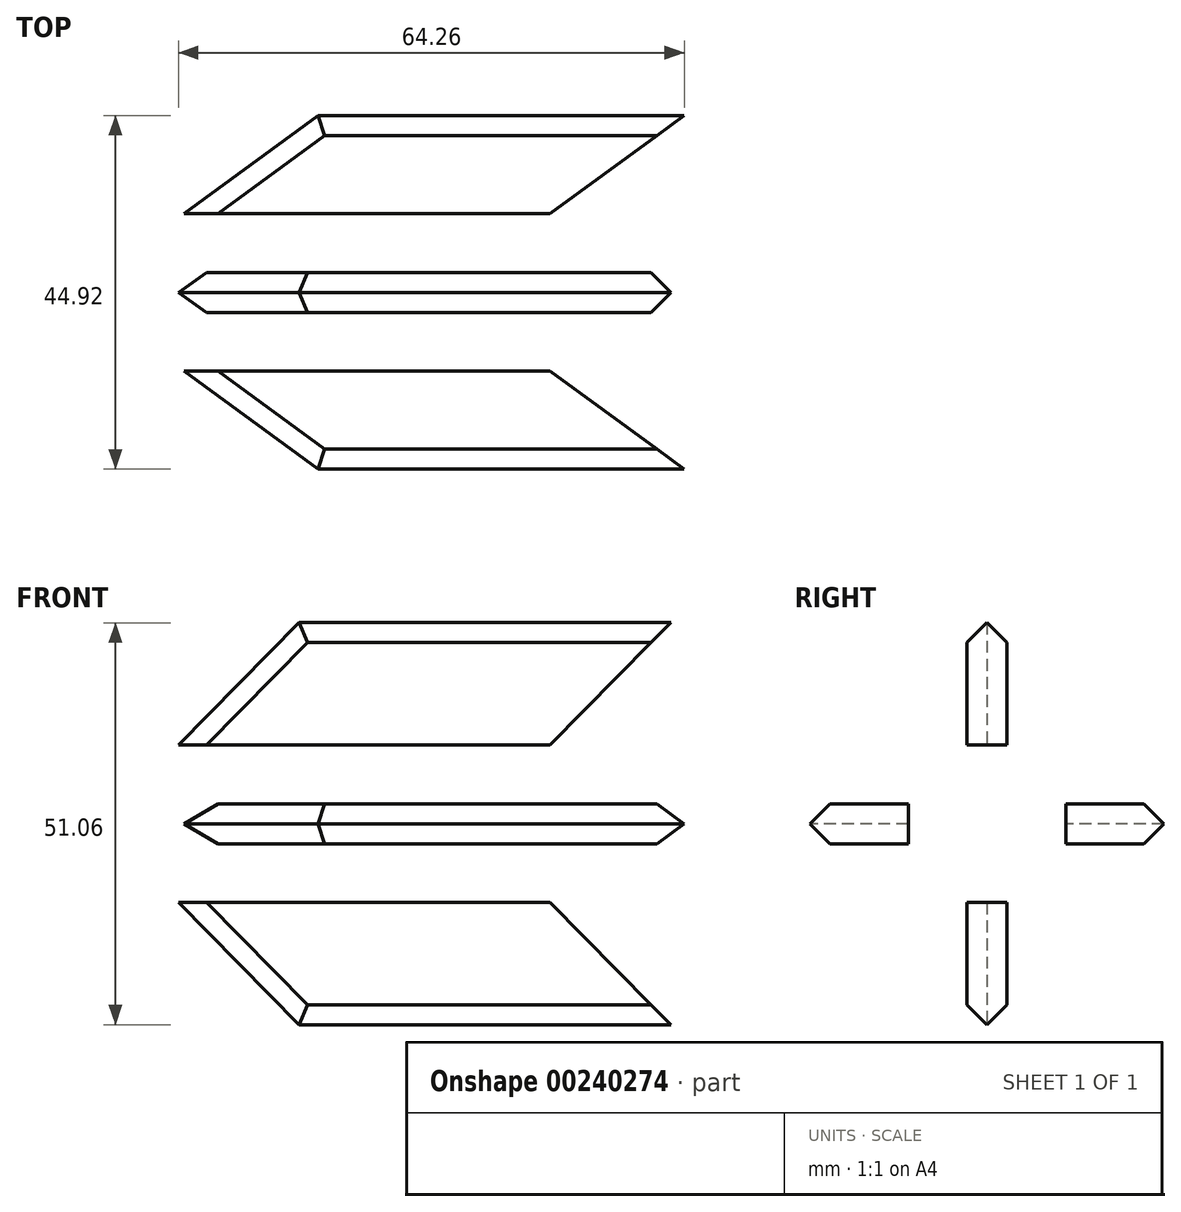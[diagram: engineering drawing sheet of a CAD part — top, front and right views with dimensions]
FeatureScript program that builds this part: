
annotation { "Feature Type Name" : "Feature", "Feature Type Description" : "" }
export const myFeature = defineFeature(function(context is Context, id is Id, definition is map)
    precondition{}
    {
        {
            var Q0;
            Q0=qCreatedBy(makeId("Top.planeOp"),FACE);
            var sketch = newSketch(context, id + "F0", { "sketchPlane" : qUnion([Q0])});
            skLineSegment(sketch, "E0.bottom", {"start": v(25.4, 10) * mm, "end": v(-25.4, 10) * mm});
            skLineSegment(sketch, "E0.top", {"start": v(25.4, -10) * mm, "end": v(-25.4, -10) * mm});
            skLineSegment(sketch, "E0.left", {"start": v(25.4, 10) * mm, "end": v(25.4, -10) * mm});
            skLineSegment(sketch, "E0.right", {"start": v(-25.4, 10) * mm, "end": v(-25.4, -10) * mm});
            skPoint(sketch, "E0.middle", {"position": v(0, 0) * mm});
            skLineSegment(sketch, "E1", {"start": v(89.65, 0) * mm, "end": v(-83.29, 0) * mm});
            skPoint(sketch, "E1.endSnap0", {"position": v(-25.4, 0) * mm});
            skLineSegment(sketch, "E2", {"start": v(-25.4, 10) * mm, "end": v(-4.9, 25) * mm});
            skLineSegment(sketch, "E3", {"start": v(-4.9, 25) * mm, "end": v(45.9, 25) * mm});
            skLineSegment(sketch, "E4", {"start": v(45.9, 25) * mm, "end": v(25.4, 10) * mm});
            skLineSegment(sketch, "E5.MirrorCS", {"start": v(-25.4, -10) * mm, "end": v(-4.9, -25) * mm});
            skLineSegment(sketch, "E6.MirrorCS", {"start": v(-4.9, -25) * mm, "end": v(45.9, -25) * mm});
            skLineSegment(sketch, "E7.MirrorCS", {"start": v(45.9, -25) * mm, "end": v(25.4, -10) * mm});
            skSolve(sketch);
        }
        {
            var Q0;
            Q0=qCreatedBy(makeId("Front.planeOp"),FACE);
            var sketch = newSketch(context, id + "F1", { "sketchPlane" : qUnion([Q0])});
            skLineSegment(sketch, "E8.bottom", {"start": v(25.4, 10) * mm, "end": v(-25.4, 10) * mm});
            skLineSegment(sketch, "E8.top", {"start": v(25.4, -10) * mm, "end": v(-25.4, -10) * mm});
            skLineSegment(sketch, "E8.left", {"start": v(25.4, 10) * mm, "end": v(25.4, -10) * mm});
            skLineSegment(sketch, "E8.right", {"start": v(-25.4, 10) * mm, "end": v(-25.4, -10) * mm});
            skPoint(sketch, "E8.middle", {"position": v(0, 0) * mm});
            skLineSegment(sketch, "E9", {"start": v(-25.4, 10) * mm, "end": v(-7.55, 28.07) * mm});
            skLineSegment(sketch, "E10", {"start": v(-7.55, 28.07) * mm, "end": v(43.25, 28.07) * mm});
            skLineSegment(sketch, "E11", {"start": v(43.25, 28.07) * mm, "end": v(25.4, 10) * mm});
            skLineSegment(sketch, "E12.MirrorCS", {"start": v(-25.4, -10) * mm, "end": v(-7.55, -28.07) * mm});
            skLineSegment(sketch, "E13.MirrorCS", {"start": v(-7.55, -28.07) * mm, "end": v(43.25, -28.07) * mm});
            skLineSegment(sketch, "E14.MirrorCS", {"start": v(43.25, -28.07) * mm, "end": v(25.4, -10) * mm});
            skSolve(sketch);
        }
        {
            var Q0;
            Q0=makeQuery(id+"F0.imprint","IMPRINT",FACE,{"disambiguationData":[TD([[makeQuery(id+"F0.imprint","IMPRINT",EDGE,{"derivedFrom":sQuery(id+"F0.wireOp",EDGE,"E0.bottom")}),-1.0]])]});
            var Q1;
            Q1=makeQuery(id+"F0.imprint","IMPRINT",FACE,{"disambiguationData":[TD([[makeQuery(id+"F0.imprint","IMPRINT",EDGE,{"derivedFrom":sQuery(id+"F0.wireOp",EDGE,"E0.top")}),1.0]])]});
            extrude(context, id + "F2", {"entities" : qUnion([Q0, Q1]), "endBound" : BoundingType.SYMMETRIC, "depth" : 5.08 * mm});
        }
        {
            var Q0;
            Q0=makeQuery(id+"F1.imprint","IMPRINT",FACE,{"disambiguationData":[TD([[makeQuery(id+"F1.imprint","IMPRINT",EDGE,{"derivedFrom":sQuery(id+"F1.wireOp",EDGE,"E8.bottom")}),-1.0]])]});
            var Q1;
            Q1=makeQuery(id+"F1.imprint","IMPRINT",FACE,{"disambiguationData":[TD([[makeQuery(id+"F1.imprint","IMPRINT",EDGE,{"derivedFrom":sQuery(id+"F1.wireOp",EDGE,"E8.top")}),1.0]])]});
            extrude(context, id + "F3", {"entities" : qUnion([Q0, Q1]), "endBound" : BoundingType.SYMMETRIC, "depth" : 5.08 * mm});
        }
        {
            var Q0;
            Q0=makeQuery(id+"F2.opExtrude","CAP_EDGE",EDGE,{"disambiguationData":[OSD([sQuery(id+"F0.wireOp",EDGE,"E6.MirrorCS")])],"isStart":true});
            var Q1;
            Q1=makeQuery(id+"F2.opExtrude","CAP_EDGE",EDGE,{"disambiguationData":[OSD([sQuery(id+"F0.wireOp",EDGE,"E6.MirrorCS")])],"isStart":false});
            var Q2;
            Q2=makeQuery(id+"F3.opExtrude","CAP_EDGE",EDGE,{"disambiguationData":[OSD([sQuery(id+"F1.wireOp",EDGE,"E10")])],"isStart":true});
            var Q3;
            Q3=makeQuery(id+"F3.opExtrude","CAP_EDGE",EDGE,{"disambiguationData":[OSD([sQuery(id+"F1.wireOp",EDGE,"E10")])],"isStart":false});
            var Q4;
            Q4=makeQuery(id+"F2.opExtrude","CAP_EDGE",EDGE,{"disambiguationData":[OSD([sQuery(id+"F0.wireOp",EDGE,"E3")])],"isStart":false});
            var Q5;
            Q5=makeQuery(id+"F2.opExtrude","CAP_EDGE",EDGE,{"disambiguationData":[OSD([sQuery(id+"F0.wireOp",EDGE,"E3")])],"isStart":true});
            var Q6;
            Q6=makeQuery(id+"F3.opExtrude","CAP_EDGE",EDGE,{"disambiguationData":[OSD([sQuery(id+"F1.wireOp",EDGE,"E13.MirrorCS")])],"isStart":true});
            var Q7;
            Q7=makeQuery(id+"F3.opExtrude","CAP_EDGE",EDGE,{"disambiguationData":[OSD([sQuery(id+"F1.wireOp",EDGE,"E13.MirrorCS")])],"isStart":false});
            chamfer(context, id + "F4", {"entities" : qUnion([Q0, Q1, Q2, Q3, Q4, Q5, Q6, Q7]), "width" : 5.08 * mm, "tangentPropagation" : true});
        }
        {
            var Q0;
            Q0=makeQuery(id+"F3.opExtrude","CAP_EDGE",EDGE,{"disambiguationData":[OSD([sQuery(id+"F1.wireOp",EDGE,"E12.MirrorCS")])],"isStart":true});
            var Q1;
            Q1=makeQuery(id+"F3.opExtrude","CAP_EDGE",EDGE,{"disambiguationData":[OSD([sQuery(id+"F1.wireOp",EDGE,"E12.MirrorCS")])],"isStart":false});
            var Q2;
            Q2=makeQuery(id+"F2.opExtrude","CAP_EDGE",EDGE,{"disambiguationData":[OSD([sQuery(id+"F0.wireOp",EDGE,"E2")])],"isStart":true});
            var Q3;
            Q3=makeQuery(id+"F2.opExtrude","CAP_EDGE",EDGE,{"disambiguationData":[OSD([sQuery(id+"F0.wireOp",EDGE,"E2")])],"isStart":false});
            var Q4;
            Q4=makeQuery(id+"F3.opExtrude","CAP_EDGE",EDGE,{"disambiguationData":[OSD([sQuery(id+"F1.wireOp",EDGE,"E9")])],"isStart":true});
            var Q5;
            Q5=makeQuery(id+"F3.opExtrude","CAP_EDGE",EDGE,{"disambiguationData":[OSD([sQuery(id+"F1.wireOp",EDGE,"E9")])],"isStart":false});
            var Q6;
            Q6=makeQuery(id+"F2.opExtrude","CAP_EDGE",EDGE,{"disambiguationData":[OSD([sQuery(id+"F0.wireOp",EDGE,"E5.MirrorCS")])],"isStart":false});
            var Q7;
            Q7=makeQuery(id+"F2.opExtrude","CAP_EDGE",EDGE,{"disambiguationData":[OSD([sQuery(id+"F0.wireOp",EDGE,"E5.MirrorCS")])],"isStart":true});
            chamfer(context, id + "F5", {"entities" : qUnion([Q0, Q1, Q2, Q3, Q4, Q5, Q6, Q7]), "width" : 5.08 * mm, "tangentPropagation" : true});
        }
    });
